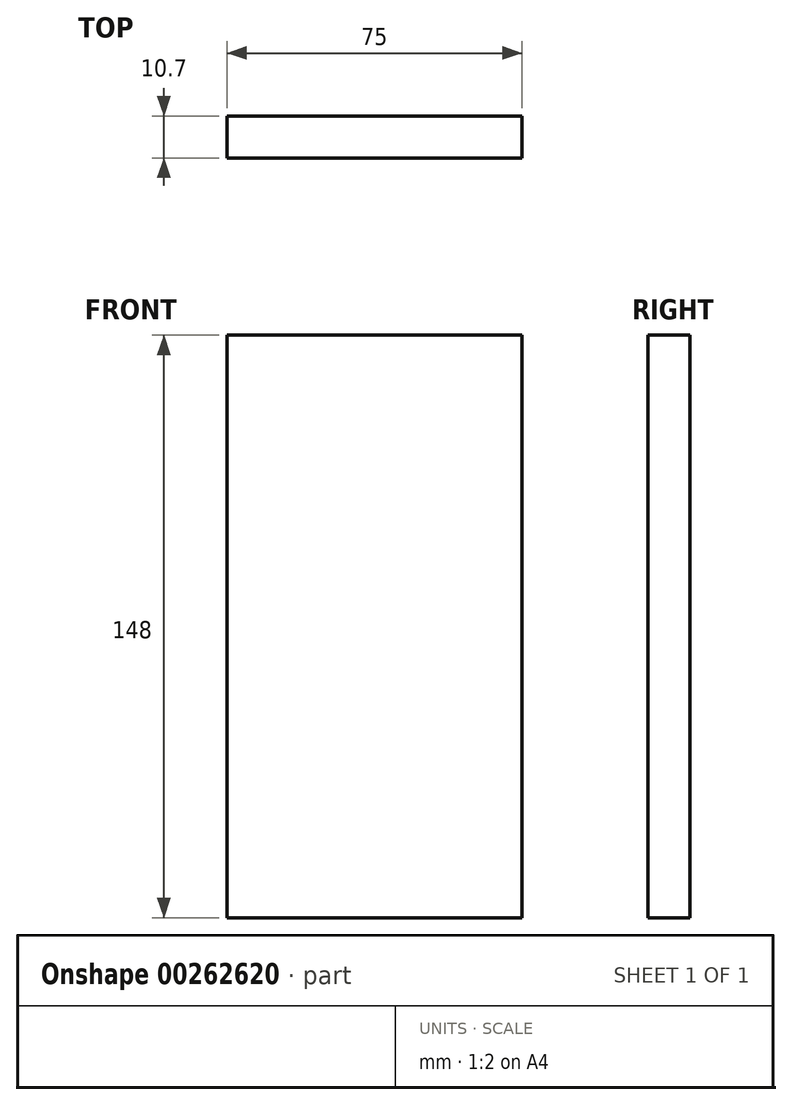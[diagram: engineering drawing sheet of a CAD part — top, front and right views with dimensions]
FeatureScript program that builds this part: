
annotation { "Feature Type Name" : "Feature", "Feature Type Description" : "" }
export const myFeature = defineFeature(function(context is Context, id is Id, definition is map)
    precondition{}
    {
        {
            var Q0;
            Q0=qCreatedBy(makeId("Front.planeOp"),FACE);
            var sketch = newSketch(context, id + "F0", { "sketchPlane" : qUnion([Q0])});
            skLineSegment(sketch, "E0.bottom", {"start": v(29.58, 76.66) * mm, "end": v(-45.42, 76.66) * mm});
            skLineSegment(sketch, "E0.top", {"start": v(29.58, -71.34) * mm, "end": v(-45.42, -71.34) * mm});
            skLineSegment(sketch, "E0.left", {"start": v(29.58, 76.66) * mm, "end": v(29.58, -71.34) * mm});
            skLineSegment(sketch, "E0.right", {"start": v(-45.42, 76.66) * mm, "end": v(-45.42, -71.34) * mm});
            skSolve(sketch);
        }
        {
            var Q0;
            Q0 = qSketchRegion(id + "F0", true);
            extrude(context, id + "F1", {"entities" : qUnion([Q0]), "depth" : 10.7 * mm});
        }
    });
